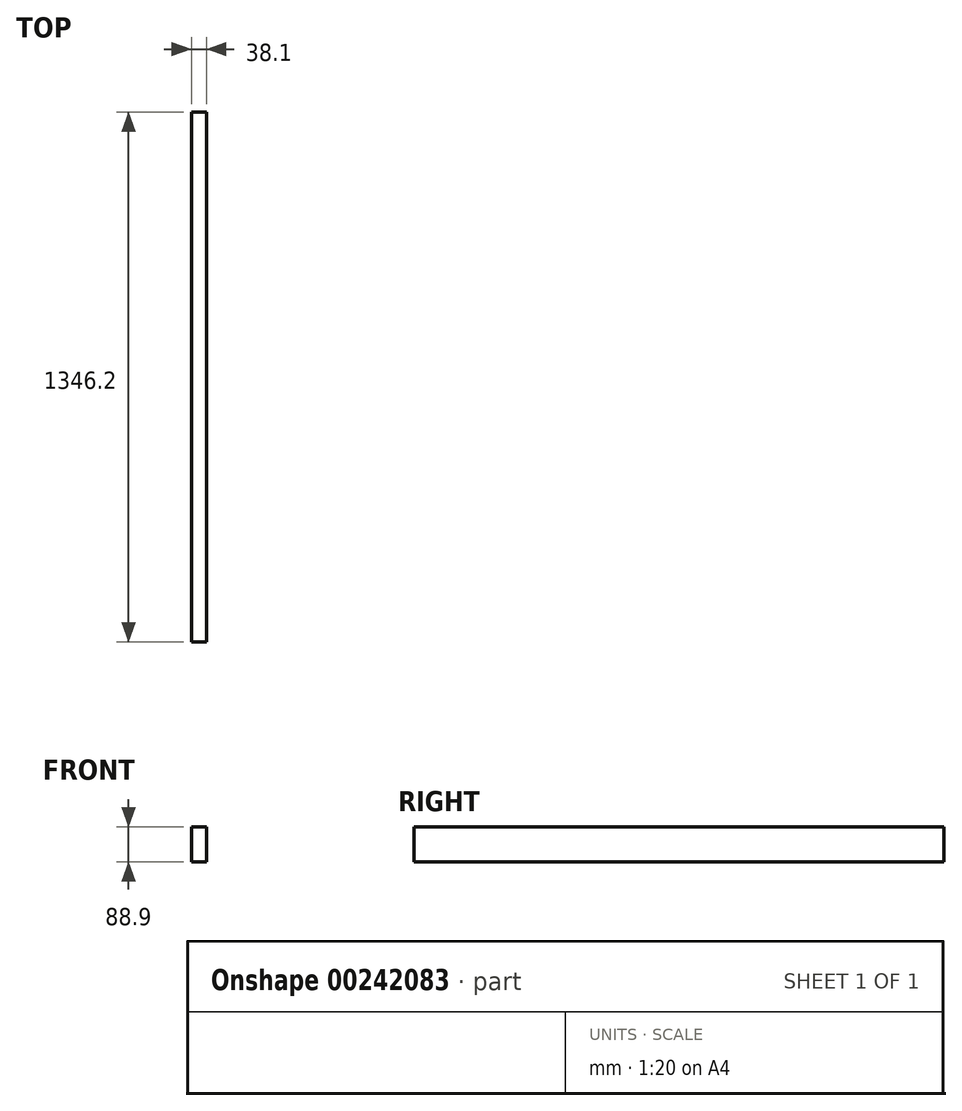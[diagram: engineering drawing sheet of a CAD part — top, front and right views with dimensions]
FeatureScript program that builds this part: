
annotation { "Feature Type Name" : "Feature", "Feature Type Description" : "" }
export const myFeature = defineFeature(function(context is Context, id is Id, definition is map)
    precondition{}
    {
        {
            var Q0;
            Q0=qCreatedBy(makeId("Front.planeOp"),FACE);
            var sketch = newSketch(context, id + "F0", { "sketchPlane" : qUnion([Q0])});
            skLineSegment(sketch, "E0.bottom", {"start": v(-29.8, 74.06) * mm, "end": v(8.3, 74.06) * mm});
            skLineSegment(sketch, "E0.top", {"start": v(-29.8, -14.84) * mm, "end": v(8.3, -14.84) * mm});
            skLineSegment(sketch, "E0.left", {"start": v(-29.8, 74.06) * mm, "end": v(-29.8, -14.84) * mm});
            skLineSegment(sketch, "E0.right", {"start": v(8.3, 74.06) * mm, "end": v(8.3, -14.84) * mm});
            skSolve(sketch);
        }
        {
            var Q0;
            Q0=makeQuery(id+"F0.imprint","IMPRINT",FACE,{"disambiguationData":[TD([[makeQuery(id+"F0.imprint","IMPRINT",EDGE,{"derivedFrom":sQuery(id+"F0.wireOp",EDGE,"E0.bottom")}),-1.0]])]});
            extrude(context, id + "F1", {"entities" : qUnion([Q0]), "depth" : 1346.2 * mm});
        }
    });
